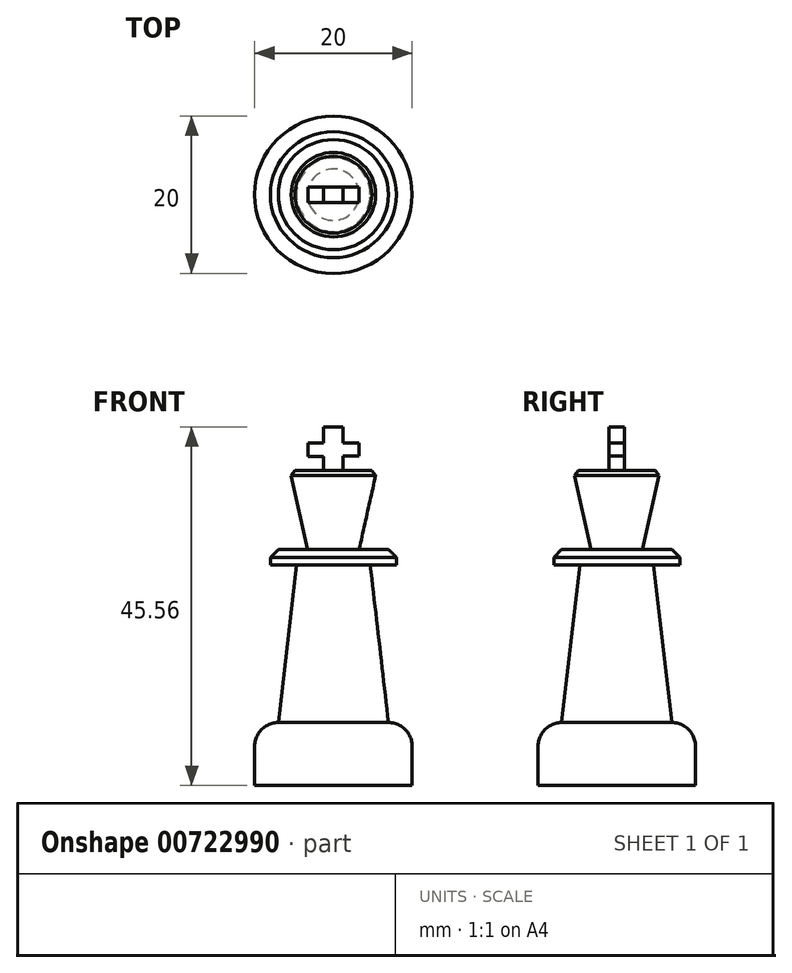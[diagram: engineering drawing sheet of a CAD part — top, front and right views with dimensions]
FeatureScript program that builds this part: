
annotation { "Feature Type Name" : "Feature", "Feature Type Description" : "" }
export const myFeature = defineFeature(function(context is Context, id is Id, definition is map)
    precondition{}
    {
        {
            var Q0;
            Q0=qCreatedBy(makeId("Top.planeOp"),FACE);
            var sketch = newSketch(context, id + "F0", { "sketchPlane" : qUnion([Q0])});
            skCircle(sketch, "E0", {"center": v(0, 0) * mm, "radius": 10 * mm});
            skSolve(sketch);
        }
        {
            var Q0;
            Q0=makeQuery(id+"F0.imprint","IMPRINT",FACE,{"disambiguationData":[TD([[makeQuery(id+"F0.imprint","IMPRINT",EDGE,{"derivedFrom":sQuery(id+"F0.wireOp",EDGE,"E0")}),1.0]])]});
            extrude(context, id + "F1", {"entities" : qUnion([Q0]), "depth" : 5 * mm, "offsetDistance" : 25 * mm});
        }
        {
            var Q0;
            Q0=makeQuery(id+"F1.opExtrude","CAP_FACE",FACE,{"disambiguationData":[OSD([sQuery(id+"F0.wireOp",EDGE,"E0")])],"isStart":false});
            extrude(context, id + "F2", {"entities" : qUnion([Q0]), "operationType" : NewBodyOperationType.ADD, "depth" : 3 * mm, "offsetDistance" : 25 * mm});
        }
        {
            var Q0;
            Q0=makeQuery(id+"F2.opExtrude","CAP_EDGE",EDGE,{"disambiguationData":[OSD([sQuery(id+"F0.wireOp",EDGE,"E0")])],"isStart":false});
            fillet(context, id + "F3", {"entities" : qUnion([Q0]), "radius" : 3 * mm, "tangentPropagation" : true, "allowEdgeOverflow" : false});
        }
        {
            var Q0;
            Q0=makeQuery(id+"F2.opExtrude","CAP_FACE",FACE,{"disambiguationData":[OSD([sQuery(id+"F0.wireOp",EDGE,"E0")])],"isStart":false});
            cPlane(context, id + "F4", {"entities" : qUnion([Q0]), "cplaneType" : CPlaneType.OFFSET, "offset" : 20 * mm, "width" : 150 * mm, "height" : 150 * mm});
        }
        {
            var Q0;
            Q0=qCreatedBy(id+"F4.planeOp",FACE);
            var sketch = newSketch(context, id + "F5", { "sketchPlane" : qUnion([Q0])});
            skPoint(sketch, "E1", {"position": v(0, 0) * mm});
            skCircle(sketch, "E2", {"center": v(0, 0) * mm, "radius": 4.68 * mm});
            skSolve(sketch);
        }
        {
            var Q1;
            Q1=makeQuery(id+"F2.opExtrude","CAP_FACE",FACE,{"disambiguationData":[OSD([sQuery(id+"F0.wireOp",EDGE,"E0")])],"isStart":false});
            var Q2;
            Q2=makeQuery(id+"F5.imprint","IMPRINT",FACE,{"disambiguationData":[TD([[makeQuery(id+"F5.imprint","IMPRINT",EDGE,{"derivedFrom":sQuery(id+"F5.wireOp",EDGE,"E2")}),1.0]])]});
            loft(context, id + "F6", {"operationType" : NewBodyOperationType.ADD, "sheetProfilesArray" : [{ "sheetProfileEntities" : qUnion([Q1]) }, { "sheetProfileEntities" : qUnion([Q2]) }]});
        }
        {
            var Q0;
            Q0=makeQuery(id+"F6.opLoft","CAP_FACE",FACE,{"disambiguationData":[OSD([makeQuery(id+"F5.imprint","IMPRINT",FACE,{"disambiguationData":[TD([[makeQuery(id+"F5.imprint","IMPRINT",EDGE,{"derivedFrom":sQuery(id+"F5.wireOp",EDGE,"E2")}),1.0]])]})])],"isStart":true});
            var sketch = newSketch(context, id + "F7", { "sketchPlane" : qUnion([Q0])});
            skCircle(sketch, "E3", {"center": v(0, 0) * mm, "radius": 8 * mm});
            skSolve(sketch);
        }
        {
            var Q0;
            Q0=makeQuery(id+"F7.imprint","IMPRINT",FACE,{"disambiguationData":[TD([[makeQuery(id+"F7.imprint","IMPRINT",EDGE,{"derivedFrom":sQuery(id+"F7.wireOp",EDGE,"E3")}),1.0]])]});
            var Q1;
            Q1=makeQuery(id+"F7.imprint","IMPRINT",FACE,{"disambiguationData":[TD([[makeQuery(id+"F7.imprint","IMPRINT",EDGE,{"derivedFrom":makeQuery(id+"F6.opLoft","MID_CAP_EDGE",EDGE,{"disambiguationData":[OSD([sQuery(id+"F5.wireOp",EDGE,"E2")])],"capPos":1.0})}),1.0]])]});
            extrude(context, id + "F8", {"entities" : qUnion([Q0, Q1]), "operationType" : NewBodyOperationType.ADD, "depth" : 2 * mm, "offsetDistance" : 25 * mm});
        }
        {
            var Q0;
            Q0=makeQuery(id+"F8.opExtrude","CAP_EDGE",EDGE,{"disambiguationData":[OSD([sQuery(id+"F7.wireOp",EDGE,"E3")])],"isStart":false});
            chamfer(context, id + "F9", {"entities" : qUnion([Q0]), "width" : 1 * mm, "tangentPropagation" : true});
        }
        {
            var Q0;
            Q0=makeQuery(id+"F8.opExtrude","CAP_FACE",FACE,{"disambiguationData":[OSD([sQuery(id+"F7.wireOp",EDGE,"E3")])],"isStart":false});
            var sketch = newSketch(context, id + "F10", { "sketchPlane" : qUnion([Q0])});
            skCircle(sketch, "E4", {"center": v(0, 0) * mm, "radius": 3.27 * mm});
            skSolve(sketch);
        }
        {
            var Q0;
            Q0=makeQuery(id+"F10.imprint","IMPRINT",FACE,{"disambiguationData":[TD([[makeQuery(id+"F10.imprint","IMPRINT",EDGE,{"derivedFrom":sQuery(id+"F10.wireOp",EDGE,"E4")}),1.0]])]});
            cPlane(context, id + "F11", {"entities" : qUnion([Q0]), "cplaneType" : CPlaneType.OFFSET, "offset" : 10 * mm, "width" : 150 * mm, "height" : 150 * mm});
        }
        {
            var Q0;
            Q0=qCreatedBy(id+"F11.planeOp",FACE);
            var sketch = newSketch(context, id + "F12", { "sketchPlane" : qUnion([Q0])});
            skCircle(sketch, "E5", {"center": v(0, 0) * mm, "radius": 5.5 * mm});
            skSolve(sketch);
        }
        {
            var Q1;
            Q1=makeQuery(id+"F10.imprint","IMPRINT",FACE,{"disambiguationData":[TD([[makeQuery(id+"F10.imprint","IMPRINT",EDGE,{"derivedFrom":sQuery(id+"F10.wireOp",EDGE,"E4")}),1.0]])]});
            var Q2;
            Q2=makeQuery(id+"F12.imprint","IMPRINT",FACE,{"disambiguationData":[TD([[makeQuery(id+"F12.imprint","IMPRINT",EDGE,{"derivedFrom":sQuery(id+"F12.wireOp",EDGE,"E5")}),1.0]])]});
            loft(context, id + "F13", {"operationType" : NewBodyOperationType.ADD, "sheetProfilesArray" : [{ "sheetProfileEntities" : qUnion([Q1]) }, { "sheetProfileEntities" : qUnion([Q2]) }]});
        }
        {
            var Q0;
            Q0=makeQuery(id+"F13.opLoft","MID_CAP_EDGE",EDGE,{"disambiguationData":[OSD([sQuery(id+"F12.wireOp",EDGE,"E5")])],"capPos":1.0});
            chamfer(context, id + "F14", {"entities" : qUnion([Q0]), "width" : 0.5 * mm, "tangentPropagation" : true});
        }
        {
            var Q0;
            Q0=qCreatedBy(makeId("Front.planeOp"),FACE);
            var sketch = newSketch(context, id + "F15", { "sketchPlane" : qUnion([Q0])});
            skLineSegment(sketch, "E6.left", {"start": v(-1.25, 39.7) * mm, "end": v(-1.25, 39.68) * mm});
            skLineSegment(sketch, "E6.right", {"start": v(1.13, 39.7) * mm, "end": v(1.13, 39.68) * mm});
            skLineSegment(sketch, "E7.bottom", {"start": v(-1.25, 39.7) * mm, "end": v(1.25, 39.7) * mm});
            skLineSegment(sketch, "E7.top", {"start": v(-1.25, 45.56) * mm, "end": v(1.25, 45.56) * mm});
            skLineSegment(sketch, "E7.left", {"start": v(-1.25, 39.7) * mm, "end": v(-1.25, 45.56) * mm});
            skLineSegment(sketch, "E7.right", {"start": v(1.25, 39.7) * mm, "end": v(1.25, 45.56) * mm});
            skPoint(sketch, "E8", {"position": v(0, 45.56) * mm});
            skPoint(sketch, "E9", {"position": v(-1.25, 42.63) * mm});
            skSolve(sketch);
        }
        {
            var Q0;
            Q0=makeQuery(id+"F15.imprint","IMPRINT",FACE,{"disambiguationData":[TD([[makeQuery(id+"F15.imprint","IMPRINT",EDGE,{"derivedFrom":sQuery(id+"F15.wireOp",EDGE,"E7.top")}),-1.0]])]});
            extrude(context, id + "F16", {"entities" : qUnion([Q0]), "operationType" : NewBodyOperationType.ADD, "depth" : 1 * mm, "offsetDistance" : 25 * mm});
        }
        {
            var Q0;
            Q0=makeQuery(id+"F16.opExtrude","CAP_FACE",FACE,{"disambiguationData":[OSD([sQuery(id+"F15.wireOp",EDGE,"E7.bottom"),sQuery(id+"F15.wireOp",EDGE,"E7.top"),sQuery(id+"F15.wireOp",EDGE,"E7.left"),sQuery(id+"F15.wireOp",EDGE,"E7.right")])],"isStart":true});
            extrude(context, id + "F17", {"entities" : qUnion([Q0]), "operationType" : NewBodyOperationType.ADD, "depth" : 1 * mm, "offsetDistance" : 25 * mm});
        }
        {
            var Q0;
            {var subQ0=sQuery(id+"F15.wireOp",EDGE,"E7.left");Q0=makeQuery(id+"F17.boolean.opBoolean","MERGE",FACE,{"derivedFrom":[makeQuery(id+"F16.opExtrude","SWEPT_FACE",FACE,{"disambiguationData":[OSD([subQ0])]}),makeQuery(id+"F17.opExtrude","SWEPT_FACE",FACE,{"disambiguationData":[OSD([subQ0])]})]});}
            var sketch = newSketch(context, id + "F18", { "sketchPlane" : qUnion([Q0])});
            skLineSegment(sketch, "E10.bottom", {"start": v(-1, 43.5) * mm, "end": v(1, 43.5) * mm});
            skLineSegment(sketch, "E10.top", {"start": v(-1, 41.82) * mm, "end": v(1, 41.82) * mm});
            skLineSegment(sketch, "E10.left", {"start": v(-1, 43.5) * mm, "end": v(-1, 41.82) * mm});
            skLineSegment(sketch, "E10.right", {"start": v(1, 43.5) * mm, "end": v(1, 41.82) * mm});
            skSolve(sketch);
        }
        {
            var Q0;
            {var subQ0=sQuery(id+"F15.wireOp",EDGE,"E7.right");Q0=makeQuery(id+"F17.boolean.opBoolean","MERGE",FACE,{"derivedFrom":[makeQuery(id+"F16.opExtrude","SWEPT_FACE",FACE,{"disambiguationData":[OSD([subQ0])]}),makeQuery(id+"F17.opExtrude","SWEPT_FACE",FACE,{"disambiguationData":[OSD([subQ0])]})]});}
            var sketch = newSketch(context, id + "F19", { "sketchPlane" : qUnion([Q0])});
            skLineSegment(sketch, "E11.bottom", {"start": v(-1, 43.52) * mm, "end": v(1, 43.52) * mm});
            skLineSegment(sketch, "E11.top", {"start": v(-1, 41.85) * mm, "end": v(1, 41.85) * mm});
            skLineSegment(sketch, "E11.left", {"start": v(-1, 43.52) * mm, "end": v(-1, 41.85) * mm});
            skLineSegment(sketch, "E11.right", {"start": v(1, 43.52) * mm, "end": v(1, 41.85) * mm});
            skSolve(sketch);
        }
        {
            var Q0;
            Q0=makeQuery(id+"F19.imprint","IMPRINT",FACE,{"disambiguationData":[TD([[makeQuery(id+"F19.imprint","IMPRINT",EDGE,{"derivedFrom":sQuery(id+"F19.wireOp",EDGE,"E11.bottom")}),-1.0]])]});
            extrude(context, id + "F20", {"entities" : qUnion([Q0]), "operationType" : NewBodyOperationType.ADD, "depth" : 2 * mm, "offsetDistance" : 25 * mm});
        }
        {
            var Q0;
            Q0=makeQuery(id+"F18.imprint","IMPRINT",FACE,{"disambiguationData":[TD([[makeQuery(id+"F18.imprint","IMPRINT",EDGE,{"derivedFrom":sQuery(id+"F18.wireOp",EDGE,"E10.bottom")}),-1.0]])]});
            extrude(context, id + "F21", {"entities" : qUnion([Q0]), "operationType" : NewBodyOperationType.ADD, "depth" : 2 * mm, "offsetDistance" : 25 * mm});
        }
    });
